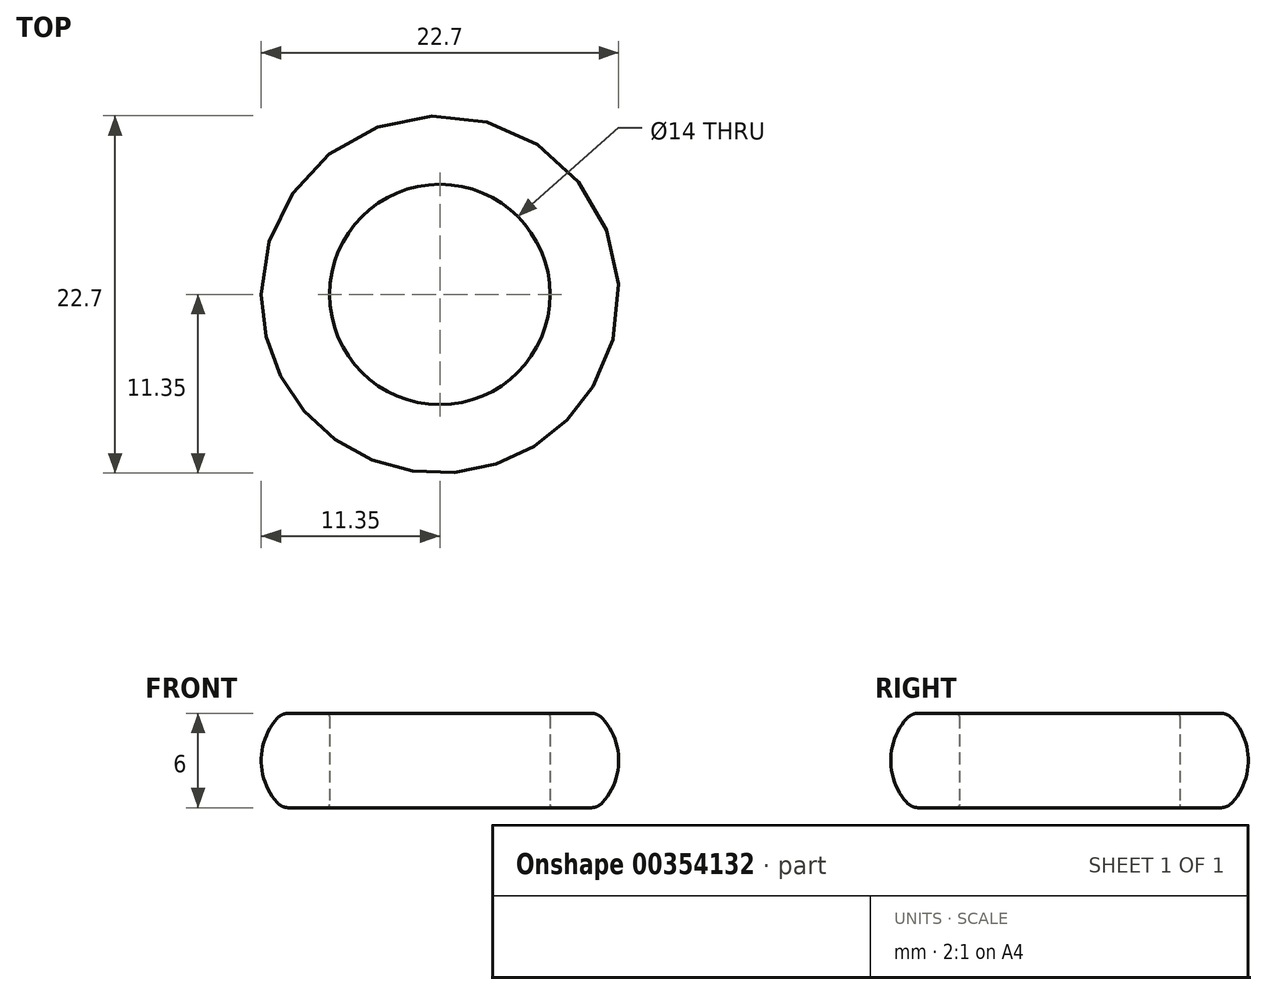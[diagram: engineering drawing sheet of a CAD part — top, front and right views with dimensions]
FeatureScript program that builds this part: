
annotation { "Feature Type Name" : "Feature", "Feature Type Description" : "" }
export const myFeature = defineFeature(function(context is Context, id is Id, definition is map)
    precondition{}
    {
        {
            var Q0;
            Q0=qCreatedBy(makeId("Front.planeOp"),FACE);
            var sketch = newSketch(context, id + "F0", { "sketchPlane" : qUnion([Q0])});
            skLineSegment(sketch, "E0", {"start": v(0, 0.2) * mm, "end": v(0, 5.8) * mm});
            skLineSegment(sketch, "E1", {"start": v(-0.2, 0) * mm, "end": v(-2.6, 0) * mm});
            skLineSegment(sketch, "E2", {"start": v(-0.2, 6) * mm, "end": v(-2.6, 6) * mm});
            skArc(sketch, "E3", {"start": v(-3.34, 5.67) * mm, "mid": v(-4.35, 3) * mm, "end": v(-3.34, 0.33) * mm});
            skPoint(sketch, "E4.visualSharp", {"position": v(-3, 6) * mm});
            skArc(sketch, "E4.filletArc", {"start": v(-2.6, 6) * mm, "mid": v(-3, 5.91) * mm, "end": v(-3.34, 5.67) * mm});
            skPoint(sketch, "E5.visualSharp", {"position": v(-3, 0) * mm});
            skArc(sketch, "E5.filletArc", {"start": v(-3.34, 0.33) * mm, "mid": v(-3, 0.09) * mm, "end": v(-2.6, 0) * mm});
            skPoint(sketch, "E6.visualSharp", {"position": v(0, 0) * mm});
            skArc(sketch, "E6.filletArc", {"start": v(-0.2, 0) * mm, "mid": v(-0.06, 0.06) * mm, "end": v(0, 0.2) * mm});
            skPoint(sketch, "E7.visualSharp", {"position": v(0, 6) * mm});
            skArc(sketch, "E7.filletArc", {"start": v(0, 5.8) * mm, "mid": v(-0.06, 5.94) * mm, "end": v(-0.2, 6) * mm});
            skLineSegment(sketch, "E8.0", {"start": v(7, 0.2) * mm, "end": v(7, 5.8) * mm});
            skSolve(sketch);
        }
        {
            var Q0;
            Q0=makeQuery(id+"F0.imprint","IMPRINT",FACE,{"disambiguationData":[TD([[makeQuery(id+"F0.imprint","IMPRINT",EDGE,{"derivedFrom":sQuery(id+"F0.wireOp",EDGE,"E0")}),1.0]])]});
            var Q1;
            Q1=sQuery(id+"F0.wireOp",EDGE,"E8.0");
            revolve(context, id + "F1", {"entities" : qUnion([Q0]), "axis" : qUnion([Q1]), "revolveType" : RevolveType.FULL});
        }
    });
